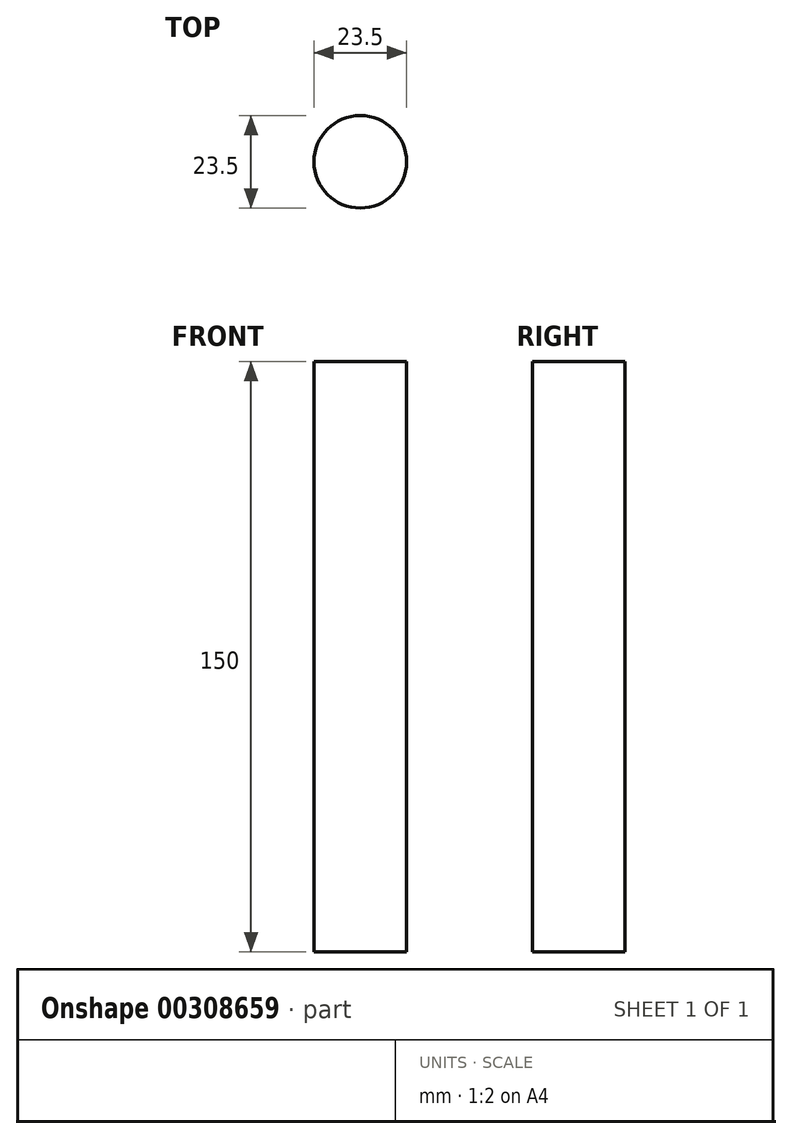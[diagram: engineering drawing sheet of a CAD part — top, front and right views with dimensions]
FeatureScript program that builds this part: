
annotation { "Feature Type Name" : "Feature", "Feature Type Description" : "" }
export const myFeature = defineFeature(function(context is Context, id is Id, definition is map)
    precondition{}
    {
        {
            var Q0;
            Q0=qCreatedBy(makeId("Top.planeOp"),FACE);
            var sketch = newSketch(context, id + "F0", { "sketchPlane" : qUnion([Q0])});
            skCircle(sketch, "E0", {"center": v(-11.75, 0) * mm, "radius": 11.75 * mm});
            skCircle(sketch, "E1.MirrorC", {"center": v(11.75, 0) * mm, "radius": 11.75 * mm});
            skSolve(sketch);
        }
        {
            var Q0;
            Q0=makeQuery(id+"F0.imprint","IMPRINT",FACE,{"disambiguationData":[TD([[makeQuery(id+"F0.imprint","IMPRINT",EDGE,{"derivedFrom":sQuery(id+"F0.wireOp",EDGE,"E1.MirrorC")}),-1.0]])]});
            var Q1;
            Q1=makeQuery(id+"F0.imprint","IMPRINT",FACE,{"disambiguationData":[TD([[makeQuery(id+"F0.imprint","IMPRINT",EDGE,{"derivedFrom":sQuery(id+"F0.wireOp",EDGE,"E0")}),1.0]])]});
            extrude(context, id + "F1", {"entities" : qUnion([Q0, Q1]), "depth" : 150 * mm});
        }
    });
